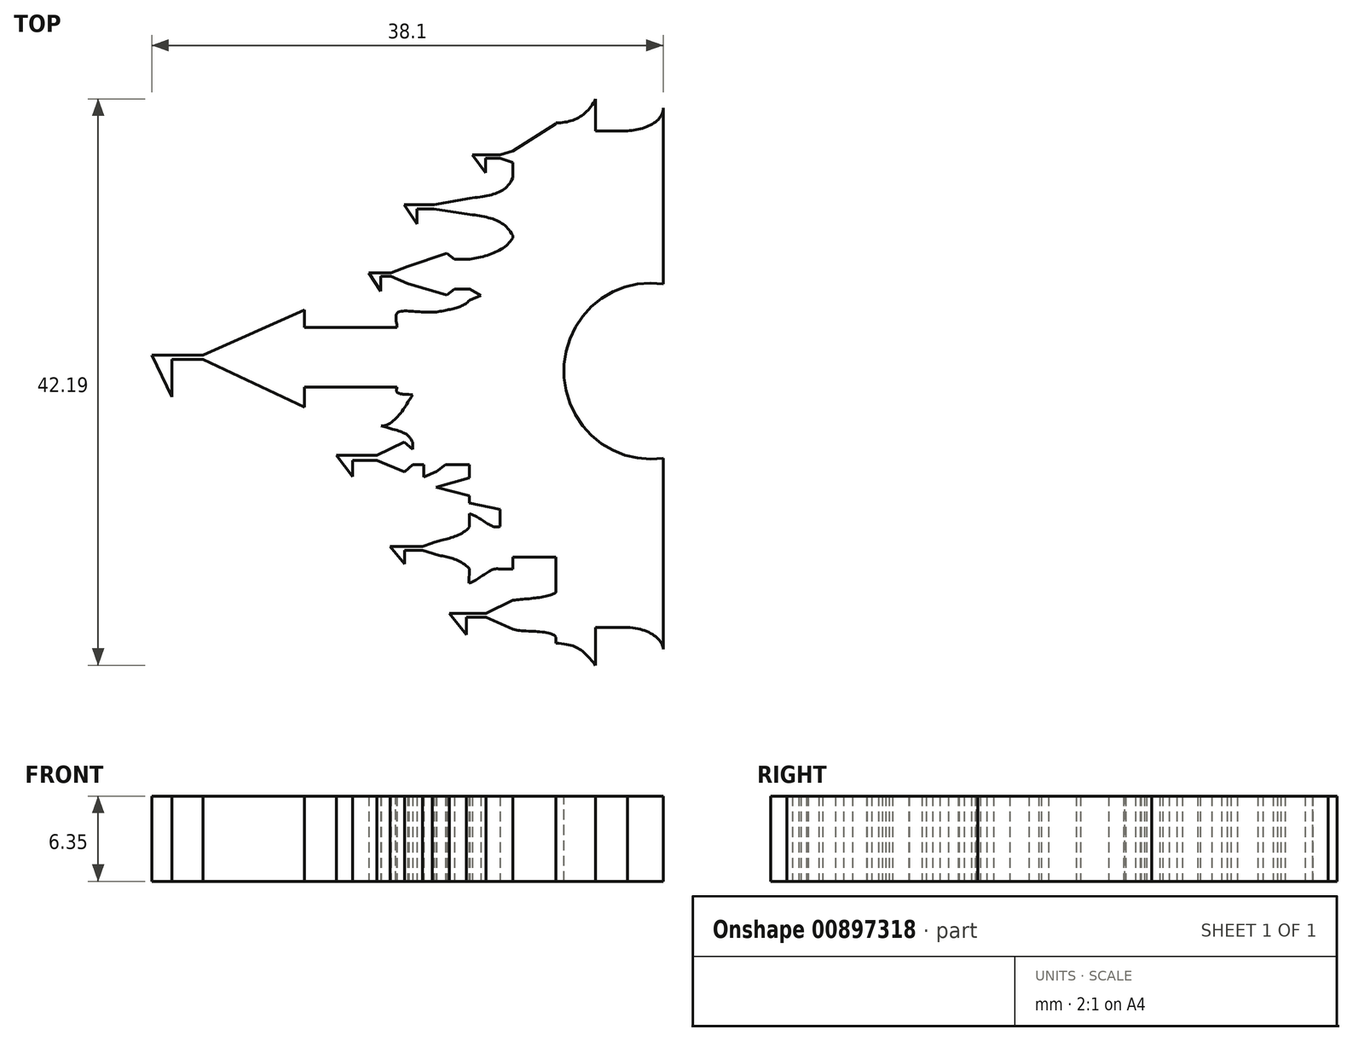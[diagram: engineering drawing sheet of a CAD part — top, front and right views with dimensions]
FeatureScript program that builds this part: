
annotation { "Feature Type Name" : "Feature", "Feature Type Description" : "" }
export const myFeature = defineFeature(function(context is Context, id is Id, definition is map)
    precondition{}
    {
        {
            var Q0;
            Q0=qCreatedBy(makeId("Top.planeOp"),FACE);
            var sketch = newSketch(context, id + "F0", { "sketchPlane" : qUnion([Q0])});
            skLineSegment(sketch, "E0.bottom", {"start": v(-4.8, 3.42) * mm, "end": v(-4.8, 3.42) * mm});
            skLineSegment(sketch, "E0.top", {"start": v(-4.8, 7.89) * mm, "end": v(0.18, 7.89) * mm});
            skLineSegment(sketch, "E0.right", {"start": v(0.18, 3.42) * mm, "end": v(0.18, 7.89) * mm});
            skLineSegment(sketch, "E1.left", {"start": v(0.18, 7.89) * mm, "end": v(0.18, 3.42) * mm});
            skLineSegment(sketch, "E1.right", {"start": v(5.03, 7.89) * mm, "end": v(5.03, -2.86) * mm});
            skLineSegment(sketch, "E2.left", {"start": v(5.03, 9.01) * mm, "end": v(5.03, -2.86) * mm});
            skLineSegment(sketch, "E2.right", {"start": v(7.52, 7.89) * mm, "end": v(7.52, -4.55) * mm});
            skLineSegment(sketch, "E3", {"start": v(7.52, 9.01) * mm, "end": v(7.52, 7.89) * mm});
            skLineSegment(sketch, "E4.bottom", {"start": v(10.71, 14.63) * mm, "end": v(10.76, 14.63) * mm});
            skLineSegment(sketch, "E4.left", {"start": v(7.52, 12.96) * mm, "end": v(7.52, 10.72) * mm});
            skLineSegment(sketch, "E4.right", {"start": v(10.76, 14.63) * mm, "end": v(10.71, -10.14) * mm});
            skLineSegment(sketch, "E5.left", {"start": v(10.71, 21.03) * mm, "end": v(10.71, -10.14) * mm});
            skLineSegment(sketch, "E5.right", {"start": v(13.93, 23.06) * mm, "end": v(13.93, -15.66) * mm});
            skLineSegment(sketch, "E6.left", {"start": v(13.93, 23.12) * mm, "end": v(13.93, -15.66) * mm});
            skLineSegment(sketch, "E6.right", {"start": v(16.9, 24.9) * mm, "end": v(16.9, 9.7) * mm});
            skLineSegment(sketch, "E7.top", {"start": v(16.9, 22.52) * mm, "end": v(19.26, 22.52) * mm});
            skLineSegment(sketch, "E7.left", {"start": v(16.9, -17.3) * mm, "end": v(16.9, -0.46) * mm});
            skLineSegment(sketch, "E7.right", {"start": v(19.26, -14.48) * mm, "end": v(19.26, -1.7) * mm});
            skLineSegment(sketch, "E8.left", {"start": v(19.26, 22.52) * mm, "end": v(19.26, 10.94) * mm});
            skLineSegment(sketch, "E8.right", {"start": v(21.93, 24.24) * mm, "end": v(21.93, 11.1) * mm});
            skFitSpline(sketch, "E9", {"points": [v(13.93, -15.66) * mm, v(16.9, -17.3) * mm], "startDerivative": vector(5.3, -0.23) * mm, "endDerivative": vector(2.67, -3.02) * mm});
            skLineSegment(sketch, "E10", {"start": v(10.71, -9.24) * mm, "end": v(13.93, -9.24) * mm});
            skLineSegment(sketch, "E11", {"start": v(16.9, -14.48) * mm, "end": v(19.26, -14.48) * mm});
            skFitSpline(sketch, "E12", {"points": [v(19.26, -14.48) * mm, v(21.93, -16.1) * mm], "startDerivative": vector(4.74, -0.1) * mm, "endDerivative": vector(0, -2.14) * mm});
            skFitSpline(sketch, "E13", {"points": [v(13.93, 23.12) * mm, v(16.9, 24.9) * mm], "startDerivative": vector(3.99, -0.07) * mm, "endDerivative": vector(1.9, 3.65) * mm});
            skFitSpline(sketch, "E14", {"points": [v(19.26, 22.52) * mm, v(21.93, 24.24) * mm], "startDerivative": vector(3.58, 0.12) * mm, "endDerivative": vector(0, 3.29) * mm});
            skLineSegment(sketch, "E15", {"start": v(4.08, -3.27) * mm, "end": v(4.08, -2.34) * mm});
            skLineSegment(sketch, "E16", {"start": v(0.18, 3.42) * mm, "end": v(2.1, 3.42) * mm});
            skFitSpline(sketch, "E17", {"points": [v(2.1, 3.42) * mm, v(2.1, 3.03) * mm, v(4.08, 2.91) * mm], "startDerivative": vector(-0.46, -1.64) * mm, "endDerivative": vector(3.52, 0.22) * mm});
            skLineSegment(sketch, "E18", {"start": v(0.18, 7.89) * mm, "end": v(2.1, 7.89) * mm});
            skFitSpline(sketch, "E19", {"points": [v(2.1, 7.89) * mm, v(2.1, 8.94) * mm, v(3.93, 9.03) * mm], "startDerivative": vector(-0.14, 2.37) * mm, "endDerivative": vector(3.17, -0.08) * mm});
            skLineSegment(sketch, "E20", {"start": v(3.93, 9.03) * mm, "end": v(5.03, 9.01) * mm});
            skFitSpline(sketch, "E21", {"points": [v(3.27, 2.86) * mm, v(0.91, 0.54) * mm], "startDerivative": vector(-1.43, -2.06) * mm, "endDerivative": vector(-3.22, 0.06) * mm});
            skFitSpline(sketch, "E22", {"points": [v(0.91, 0.54) * mm, v(3.27, -0.68) * mm], "startDerivative": vector(5.86, -1.61) * mm, "endDerivative": vector(1.2, -2.04) * mm});
            skLineSegment(sketch, "E23", {"start": v(3.27, -0.68) * mm, "end": v(3.27, -1.2) * mm});
            skLineSegment(sketch, "E24", {"start": v(2.63, -0.68) * mm, "end": v(0.61, -1.65) * mm});
            skLineSegment(sketch, "E25", {"start": v(0.61, -2.04) * mm, "end": v(2.65, -2.88) * mm});
            skLineSegment(sketch, "E26", {"start": v(2.65, -2.88) * mm, "end": v(3.27, -2.34) * mm});
            skLineSegment(sketch, "E27", {"start": v(3.27, -2.34) * mm, "end": v(4.08, -2.34) * mm});
            skLineSegment(sketch, "E28", {"start": v(3.27, -1.2) * mm, "end": v(2.63, -0.68) * mm});
            skLineSegment(sketch, "E29", {"start": v(4.08, -3.27) * mm, "end": v(5.03, -2.86) * mm});
            skLineSegment(sketch, "E30", {"start": v(5.03, -2.86) * mm, "end": v(5.72, -2.34) * mm});
            skLineSegment(sketch, "E31", {"start": v(5.72, -2.34) * mm, "end": v(7.49, -2.34) * mm});
            skFitSpline(sketch, "E32", {"points": [v(5.03, 9.01) * mm, v(7.51, 9.9) * mm], "startDerivative": vector(3.2, 0.7) * mm, "endDerivative": vector(1.67, 1.86) * mm});
            skLineSegment(sketch, "E33", {"start": v(7.49, -4.68) * mm, "end": v(5, -4.04) * mm});
            skLineSegment(sketch, "E34", {"start": v(5, -4.04) * mm, "end": v(7.52, -3.32) * mm});
            skLineSegment(sketch, "E35", {"start": v(7.48, -5.21) * mm, "end": v(9.77, -5.68) * mm});
            skLineSegment(sketch, "E36", {"start": v(9.77, -5.68) * mm, "end": v(9.77, -6.95) * mm});
            skFitSpline(sketch, "E37", {"points": [v(9.77, -6.95) * mm, v(7.48, -6) * mm], "startDerivative": vector(-1.86, -0.86) * mm, "endDerivative": vector(-2.44, 0.57) * mm});
            skFitSpline(sketch, "E38", {"points": [v(7.48, -7) * mm, v(4.72, -8.2) * mm], "startDerivative": vector(-2.1, -2.57) * mm, "endDerivative": vector(-1.86, -0.86) * mm});
            skFitSpline(sketch, "E39", {"points": [v(7.47, -10.1) * mm, v(4.72, -8.95) * mm], "startDerivative": vector(-2.53, 2.72) * mm, "endDerivative": vector(-2.14, 0.86) * mm});
            skLineSegment(sketch, "E40", {"start": v(4.72, -8.2) * mm, "end": v(4.72, -8.95) * mm});
            skLineSegment(sketch, "E41", {"start": v(4.72, -8.95) * mm, "end": v(4, -8.73) * mm});
            skLineSegment(sketch, "E42", {"start": v(4, -8.46) * mm, "end": v(4.72, -8.2) * mm});
            skFitSpline(sketch, "E43", {"points": [v(7.47, -11.2) * mm, v(9.77, -10.14) * mm], "startDerivative": vector(2.89, 1.14) * mm, "endDerivative": vector(2, -0.71) * mm});
            skLineSegment(sketch, "E44", {"start": v(9.77, -10.14) * mm, "end": v(10.71, -10.14) * mm});
            skLineSegment(sketch, "E45.trimOffspring", {"start": v(7.48, -6) * mm, "end": v(7.47, -11.2) * mm});
            skLineSegment(sketch, "E46", {"start": v(7.51, 9.9) * mm, "end": v(8.34, 10.24) * mm});
            skLineSegment(sketch, "E47", {"start": v(8.34, 10.24) * mm, "end": v(7.52, 10.72) * mm});
            skLineSegment(sketch, "E48", {"start": v(7.52, 10.72) * mm, "end": v(6.39, 10.72) * mm});
            skLineSegment(sketch, "E49", {"start": v(6.39, 10.72) * mm, "end": v(5.82, 10.3) * mm});
            skLineSegment(sketch, "E50", {"start": v(5.82, 10.3) * mm, "end": v(2.87, 11.15) * mm});
            skLineSegment(sketch, "E51", {"start": v(2.87, 11.15) * mm, "end": v(2.87, 12.4) * mm});
            skLineSegment(sketch, "E52", {"start": v(2.87, 12.4) * mm, "end": v(5.82, 13.39) * mm});
            skLineSegment(sketch, "E53", {"start": v(5.82, 13.39) * mm, "end": v(6.39, 12.96) * mm});
            skLineSegment(sketch, "E54", {"start": v(6.39, 12.96) * mm, "end": v(7.52, 12.96) * mm});
            skLineSegment(sketch, "E55", {"start": v(2.87, 11.15) * mm, "end": v(1.65, 11.7) * mm});
            skLineSegment(sketch, "E56", {"start": v(2.87, 12.4) * mm, "end": v(1.65, 11.93) * mm});
            skLineSegment(sketch, "E57.trimOffspring", {"start": v(7.51, 9.9) * mm, "end": v(7.48, -5.21) * mm});
            skFitSpline(sketch, "E58", {"points": [v(7.52, 12.96) * mm, v(10.76, 14.63) * mm], "startDerivative": vector(3.74, 0.57) * mm, "endDerivative": vector(1.56, 3.14) * mm});
            skFitSpline(sketch, "E59", {"points": [v(10.76, 14.63) * mm, v(7.52, 16.3) * mm], "startDerivative": vector(-1.7, 3.72) * mm, "endDerivative": vector(-4.45, 0.57) * mm});
            skLineSegment(sketch, "E60", {"start": v(7.52, 16.3) * mm, "end": v(7.52, 17.48) * mm});
            skFitSpline(sketch, "E61", {"points": [v(7.52, 17.48) * mm, v(10.71, 19) * mm], "startDerivative": vector(4.6, 0.71) * mm, "endDerivative": vector(1.55, 3.72) * mm});
            skLineSegment(sketch, "E62", {"start": v(7.52, 16.3) * mm, "end": v(4.85, 16.7) * mm});
            skLineSegment(sketch, "E63", {"start": v(4.85, 17) * mm, "end": v(7.52, 17.48) * mm});
            skPoint(sketch, "E64.trimOffspring.end.orphan", {"position": v(3.93, 3.42) * mm});
            skLineSegment(sketch, "E65", {"start": v(3.27, 2.86) * mm, "end": v(3, 2.88) * mm});
            skLineSegment(sketch, "E66", {"start": v(10.71, 19) * mm, "end": v(11.5, 19.59) * mm});
            skLineSegment(sketch, "E67", {"start": v(11.5, 19.59) * mm, "end": v(10.71, 20.15) * mm});
            skLineSegment(sketch, "E68", {"start": v(10.71, 21.03) * mm, "end": v(13.93, 23.06) * mm});
            skLineSegment(sketch, "E69", {"start": v(10.71, 20.15) * mm, "end": v(9.77, 20.46) * mm});
            skLineSegment(sketch, "E70", {"start": v(9.77, 20.73) * mm, "end": v(10.71, 21.03) * mm});
            skEllipticalArc(sketch, "E71", {});
            skPoint(sketch, "E72.start.orphan", {"position": v(14.52, 4.47) * mm});
            skLineSegment(sketch, "E73.trimOffspring", {"start": v(16.9, -0.46) * mm, "end": v(16.9, -14.48) * mm});
            skLineSegment(sketch, "E74.trimOffspring", {"start": v(16.9, 9.7) * mm, "end": v(16.9, 22.52) * mm});
            skLineSegment(sketch, "E75.trimOffspring", {"start": v(19.26, 10.94) * mm, "end": v(19.26, 22.52) * mm});
            skLineSegment(sketch, "E76.trimOffspring", {"start": v(21.93, -1.86) * mm, "end": v(21.93, -16.1) * mm});
            skLineSegment(sketch, "E77.trimOffspring", {"start": v(19.26, -1.7) * mm, "end": v(19.26, -14.48) * mm});
            skFitSpline(sketch, "E78", {"points": [v(13.93, -15.2) * mm, v(10.74, -14.6) * mm], "startDerivative": vector(-1.11, 1.78) * mm, "endDerivative": vector(-2.38, 0.83) * mm});
            skFitSpline(sketch, "E79", {"points": [v(13.93, -11.87) * mm, v(10.74, -12.46) * mm], "startDerivative": vector(-2, -1.34) * mm, "endDerivative": vector(-3.12, -0.45) * mm});
            skLineSegment(sketch, "E80", {"start": v(10.74, -14.6) * mm, "end": v(10.74, -12.46) * mm});
            skLineSegment(sketch, "E81", {"start": v(10.74, -14.6) * mm, "end": v(8.73, -13.71) * mm});
            skLineSegment(sketch, "E82", {"start": v(8.73, -13.42) * mm, "end": v(10.74, -12.46) * mm});
            skLineSegment(sketch, "E83", {"start": v(-4.8, 1.95) * mm, "end": v(-4.8, 3.42) * mm});
            skLineSegment(sketch, "E84", {"start": v(-4.8, 9.17) * mm, "end": v(-12.34, 5.8) * mm});
            skLineSegment(sketch, "E85", {"start": v(-12.34, 5.5) * mm, "end": v(-4.8, 1.95) * mm});
            skLineSegment(sketch, "E86", {"start": v(-4.8, 7.89) * mm, "end": v(-4.8, 9.17) * mm});
            skLineSegment(sketch, "E87", {"start": v(-4.8, 3.42) * mm, "end": v(0.18, 3.42) * mm});
            skLineSegment(sketch, "E88", {"start": v(-12.34, 5.5) * mm, "end": v(-14.66, 5.5) * mm});
            skLineSegment(sketch, "E89", {"start": v(-12.34, 5.8) * mm, "end": v(-14.66, 5.8) * mm});
            skLineSegment(sketch, "E90", {"start": v(-14.66, 5.5) * mm, "end": v(-14.66, 2.7) * mm});
            skLineSegment(sketch, "E91", {"start": v(-14.66, 2.7) * mm, "end": v(-16.17, 5.8) * mm});
            skLineSegment(sketch, "E92", {"start": v(-16.17, 5.8) * mm, "end": v(-14.66, 5.8) * mm});
            skLineSegment(sketch, "E93", {"start": v(1.65, 11.7) * mm, "end": v(0.89, 11.7) * mm});
            skLineSegment(sketch, "E94", {"start": v(1.65, 11.93) * mm, "end": v(0.89, 11.93) * mm});
            skLineSegment(sketch, "E95", {"start": v(0.89, 11.93) * mm, "end": v(0, 11.93) * mm});
            skLineSegment(sketch, "E96", {"start": v(0, 11.93) * mm, "end": v(0.89, 10.57) * mm});
            skLineSegment(sketch, "E97", {"start": v(0.89, 10.57) * mm, "end": v(0.89, 11.7) * mm});
            skLineSegment(sketch, "E98", {"start": v(4.85, 16.7) * mm, "end": v(3.6, 16.7) * mm});
            skLineSegment(sketch, "E99", {"start": v(4.85, 17) * mm, "end": v(3.87, 17) * mm});
            skLineSegment(sketch, "E100", {"start": v(3.87, 17) * mm, "end": v(2.62, 17) * mm});
            skLineSegment(sketch, "E101", {"start": v(2.62, 17) * mm, "end": v(3.6, 15.58) * mm});
            skLineSegment(sketch, "E102", {"start": v(3.6, 15.58) * mm, "end": v(3.6, 16.7) * mm});
            skLineSegment(sketch, "E103", {"start": v(9.77, 20.46) * mm, "end": v(8.71, 20.46) * mm});
            skLineSegment(sketch, "E104", {"start": v(9.77, 20.73) * mm, "end": v(8.71, 20.73) * mm});
            skLineSegment(sketch, "E105", {"start": v(8.71, 20.73) * mm, "end": v(7.7, 20.73) * mm});
            skLineSegment(sketch, "E106", {"start": v(7.7, 20.73) * mm, "end": v(8.71, 19.4) * mm});
            skLineSegment(sketch, "E107", {"start": v(8.71, 19.4) * mm, "end": v(8.71, 20.46) * mm});
            skLineSegment(sketch, "E108", {"start": v(4, -8.73) * mm, "end": v(2.67, -8.73) * mm});
            skLineSegment(sketch, "E109", {"start": v(4, -8.46) * mm, "end": v(2.67, -8.46) * mm});
            skLineSegment(sketch, "E110", {"start": v(2.67, -8.46) * mm, "end": v(1.59, -8.46) * mm});
            skLineSegment(sketch, "E111", {"start": v(1.59, -8.46) * mm, "end": v(2.67, -9.76) * mm});
            skLineSegment(sketch, "E112", {"start": v(2.67, -9.76) * mm, "end": v(2.67, -8.73) * mm});
            skLineSegment(sketch, "E113", {"start": v(8.73, -13.71) * mm, "end": v(7.26, -13.71) * mm});
            skLineSegment(sketch, "E114", {"start": v(8.73, -13.42) * mm, "end": v(7.26, -13.42) * mm});
            skLineSegment(sketch, "E115", {"start": v(7.26, -13.42) * mm, "end": v(6.01, -13.42) * mm});
            skLineSegment(sketch, "E116", {"start": v(6.01, -13.42) * mm, "end": v(7.26, -15.03) * mm});
            skLineSegment(sketch, "E117", {"start": v(7.26, -15.03) * mm, "end": v(7.26, -13.71) * mm});
            skLineSegment(sketch, "E118", {"start": v(0.61, -2.04) * mm, "end": v(-1.23, -2.04) * mm});
            skLineSegment(sketch, "E119", {"start": v(0.61, -1.65) * mm, "end": v(-1.23, -1.65) * mm});
            skLineSegment(sketch, "E120", {"start": v(-1.23, -1.65) * mm, "end": v(-2.43, -1.65) * mm});
            skLineSegment(sketch, "E121", {"start": v(-2.43, -1.65) * mm, "end": v(-1.23, -3.25) * mm});
            skLineSegment(sketch, "E122", {"start": v(-1.23, -3.25) * mm, "end": v(-1.23, -2.04) * mm});
            const initialGuessF0  = {"E71": [0.020987177213165, 0.00462191626950754, -0.9997358683659497, -0.022982460759901825, 0.006464069382781946, 0.006555589933720385, 4.542137550806313, 1.6944281768725864]};
            skSetInitialGuess(sketch, initialGuessF0);
            skSolve(sketch);
        }
        {
            var Q0;
            Q0 = qSketchRegion(id + "F0", true);
            extrude(context, id + "F1", {"entities" : qUnion([Q0]), "depth" : 6.35 * mm, "offsetDistance" : 25.4 * mm});
        }
    });
